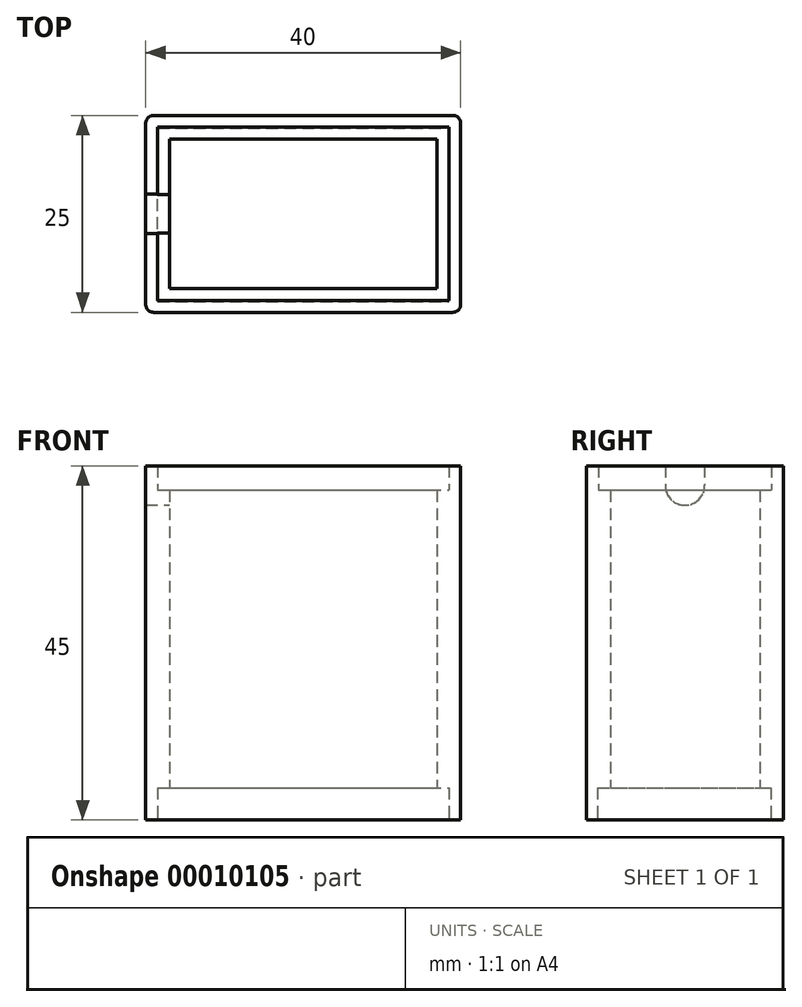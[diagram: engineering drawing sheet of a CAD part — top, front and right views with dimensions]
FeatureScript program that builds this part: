
annotation { "Feature Type Name" : "Feature", "Feature Type Description" : "" }
export const myFeature = defineFeature(function(context is Context, id is Id, definition is map)
    precondition{}
    {
        {
            var Q0;
            Q0=qCreatedBy(makeId("Top.planeOp"),FACE);
            var sketch = newSketch(context, id + "F0", { "sketchPlane" : qUnion([Q0])});
            skLineSegment(sketch, "E0.rect.bottom", {"start": v(20, 12.5) * mm, "end": v(-20, 12.5) * mm});
            skLineSegment(sketch, "E0.rect.top", {"start": v(20, -12.5) * mm, "end": v(-20, -12.5) * mm});
            skLineSegment(sketch, "E0.rect.left", {"start": v(20, 12.5) * mm, "end": v(20, -12.5) * mm});
            skLineSegment(sketch, "E0.rect.right", {"start": v(-20, 12.5) * mm, "end": v(-20, -12.5) * mm});
            skPoint(sketch, "E0.rect.middle", {"position": v(0, 0) * mm});
            skLineSegment(sketch, "E1.rect.bottom", {"start": v(17, 9.5) * mm, "end": v(-17, 9.5) * mm});
            skLineSegment(sketch, "E1.rect.top", {"start": v(17, -9.5) * mm, "end": v(-17, -9.5) * mm});
            skLineSegment(sketch, "E1.rect.left", {"start": v(17, 9.5) * mm, "end": v(17, -9.5) * mm});
            skLineSegment(sketch, "E1.rect.right", {"start": v(-17, 9.5) * mm, "end": v(-17, -9.5) * mm});
            skLineSegment(sketch, "E2", {"start": v(20, -3.98) * mm, "end": v(17, -3.98) * mm, "construction": true});
            skLineSegment(sketch, "E3", {"start": v(16.8, 12.5) * mm, "end": v(16.8, 9.5) * mm, "construction": true});
            skSolve(sketch);
        }
        {
            var Q0;
            Q0=makeQuery(id+"F0.imprint","IMPRINT",FACE,{"disambiguationData":[TD([[makeQuery(id+"F0.imprint","IMPRINT",EDGE,{"derivedFrom":sQuery(id+"F0.wireOp",EDGE,"E0.rect.bottom")}),1.0]])]});
            extrude(context, id + "F1", {"entities" : qUnion([Q0]), "depth" : 45 * mm});
        }
        {
            var Q0;
            Q0=makeQuery(id+"F1.opExtrude","SWEPT_EDGE",EDGE,{"disambiguationData":[OSD([sQuery(id+"F0.wireOp",EDGE,"E0.rect.bottom"),sQuery(id+"F0.wireOp",EDGE,"E0.rect.right")])]});
            var Q1;
            Q1=makeQuery(id+"F1.opExtrude","SWEPT_EDGE",EDGE,{"disambiguationData":[OSD([sQuery(id+"F0.wireOp",EDGE,"E0.rect.bottom"),sQuery(id+"F0.wireOp",EDGE,"E0.rect.left")])]});
            var Q2;
            Q2=makeQuery(id+"F1.opExtrude","SWEPT_EDGE",EDGE,{"disambiguationData":[OSD([sQuery(id+"F0.wireOp",EDGE,"E0.rect.top"),sQuery(id+"F0.wireOp",EDGE,"E0.rect.right")])]});
            var Q3;
            Q3=makeQuery(id+"F1.opExtrude","SWEPT_EDGE",EDGE,{"disambiguationData":[OSD([sQuery(id+"F0.wireOp",EDGE,"E0.rect.top"),sQuery(id+"F0.wireOp",EDGE,"E0.rect.left")])]});
            fillet(context, id + "F2", {"entities" : qUnion([Q0, Q1, Q2, Q3]), "radius" : 1 * mm, "tangentPropagation" : true, "allowEdgeOverflow" : false});
        }
        {
            var Q0;
            Q0=qCreatedBy(makeId("Right.planeOp"),FACE);
            var sketch = newSketch(context, id + "F3", { "sketchPlane" : qUnion([Q0])});
            skLineSegment(sketch, "E4.rect.bottom", {"start": v(-11, 62.38) * mm, "end": v(11, 62.38) * mm});
            skLineSegment(sketch, "E4.rect.top", {"start": v(-11, 41.9) * mm, "end": v(11, 41.9) * mm});
            skLineSegment(sketch, "E4.rect.left", {"start": v(-11, 62.38) * mm, "end": v(-11, 41.9) * mm});
            skLineSegment(sketch, "E4.rect.right", {"start": v(11, 62.38) * mm, "end": v(11, 41.9) * mm});
            skPoint(sketch, "E4.rect.middle", {"position": v(0, 52.14) * mm});
            skLineSegment(sketch, "E5", {"start": v(0, 41.9) * mm, "end": v(0, 0) * mm, "construction": true});
            skLineSegment(sketch, "E6.rect.bottom", {"start": v(-11.11, 4.1) * mm, "end": v(10.89, 4.1) * mm});
            skLineSegment(sketch, "E6.rect.top", {"start": v(-11.11, 0) * mm, "end": v(10.89, 0) * mm});
            skLineSegment(sketch, "E6.rect.left", {"start": v(-11.11, 4.1) * mm, "end": v(-11.11, 0) * mm});
            skLineSegment(sketch, "E6.rect.right", {"start": v(10.89, 4.1) * mm, "end": v(10.89, 0) * mm});
            skPoint(sketch, "E6.rect.middle", {"position": v(0, 0) * mm});
            skSolve(sketch);
        }
        {
            var Q0;
            Q0=makeQuery(id+"F3.imprint","IMPRINT",FACE,{"disambiguationData":[TD([[makeQuery(id+"F3.imprint","IMPRINT",EDGE,{"derivedFrom":sQuery(id+"F3.wireOp",EDGE,"E4.rect.bottom")}),-1.0]])]});
            var Q1;
            Q1=makeQuery(id+"F3.imprint","IMPRINT",FACE,{"disambiguationData":[TD([[makeQuery(id+"F3.imprint","IMPRINT",EDGE,{"derivedFrom":sQuery(id+"F3.wireOp",EDGE,"E6.rect.bottom")}),-1.0]])]});
            extrude(context, id + "F4", {"entities" : qUnion([Q0, Q1]), "operationType" : NewBodyOperationType.REMOVE, "endBound" : BoundingType.SYMMETRIC, "oppositeDirection" : true, "depth" : 37 * mm});
        }
        {
            var Q0;
            Q0=qCreatedBy(makeId("Right.planeOp"),FACE);
            var sketch = newSketch(context, id + "F5", { "sketchPlane" : qUnion([Q0])});
            skLineSegment(sketch, "E7", {"start": v(0, 45) * mm, "end": v(2.5, 45) * mm});
            skLineSegment(sketch, "E8", {"start": v(2.5, 45) * mm, "end": v(2.5, 42.5) * mm});
            skArc(sketch, "E9", {"start": v(2.5, 42.5) * mm, "mid": v(1.77, 40.73) * mm, "end": v(0, 40) * mm});
            skLineSegment(sketch, "E10.0.MirrorCS", {"start": v(0, 45) * mm, "end": v(-2.5, 45) * mm});
            skLineSegment(sketch, "E11.0.MirrorCS", {"start": v(-2.5, 45) * mm, "end": v(-2.5, 42.5) * mm});
            skArc(sketch, "E12.0.MirrorCS", {"start": v(-2.5, 42.5) * mm, "mid": v(-1.77, 40.73) * mm, "end": v(0, 40) * mm});
            skLineSegment(sketch, "E13", {"start": v(0, 45) * mm, "end": v(0, 0) * mm, "construction": true});
            skSolve(sketch);
        }
        {
            var Q0;
            Q0=makeQuery(id+"F5.imprint","IMPRINT",FACE,{"disambiguationData":[TD([[makeQuery(id+"F5.imprint","IMPRINT",EDGE,{"derivedFrom":sQuery(id+"F5.wireOp",EDGE,"E7")}),-1.0]])]});
            extrude(context, id + "F6", {"entities" : qUnion([Q0]), "operationType" : NewBodyOperationType.REMOVE, "oppositeDirection" : true, "depth" : 87.81 * mm});
        }
    });
